# Revit family: Domotics-DomesticRanges-GEWISS-SYSTEM_ENCLOSURE-WATERTIGHT-IP65
name_source: partatom
category: Apparecchi elettrici
revit_build: Autodesk Revit 2016 (Build: 20161004_0715(x64)
units: mm (PartAtom-declared; Revit-internal decimal feet)

## family parameters
Condiviso = No
Host = Superficie
Mantenere orientamento annotazione = Sì
Punto di calcolo locali = Sì
Quota connettore circolare = Usa diametro
Taglio con vuoti quando caricato = No
Tipo di parte = Normale

## types (1)
- Domotics-DomesticRanges-GEWISS-SYSTEM_ENCLOSURE-WATERTIGHT-IP65
    Catalogue = DOMOTICS
    Catalogue Range = SYSTEM - BOXES
    Colour = Grey RAL 7035
    Description: = 2 gang
    Descrizione = WAT. IP65 ENCLOSURE 2M RIGID TRAN. COVER
    Door colour: = Smoked Transparent
    Door type = Rigid
    EAN code = 8011564856745
    Electrocod = 0212
    Glow Wire Test = 650°C
    IDF = 5ff36bd7-3460-49dc-94cf-c3dae0df500e
    IDT = 8f8934d9-406d-40ac-8908-5aafbfcae389
    IP degree = IP65
    Immagine tipo = GW27062.jpg
    Installation temperature = -25 +60 °C
    Insulation class = II
    Lid screws = Stainless steel
    Modello = GW27062
    N. holes Ã˜ 23 with cable gland = 1
    No. knockout holes Ã˜ 23 = 3
    No. knockout holes Ã˜23 = 4 on sides / 1 on the bottom
    Outer dim. LxHxD (mm) = 66x82x65
    Produttore = GEWISS S.p.A.
    Prospetto di default = 1219 mm
    SEO = Enclosure
    Shock resistance = IK07
    Standard = EN 60670-1
    Standard; = EN 60670-1
    Technical sheet = https://www.gewiss.com
    Thermo-pressure with ball = 70
    Torque screws tightening = 0,8NM
    Type of knockout holes = Removable with tool
    URL = https://www.gewiss.com
    Version file RFA = 19.4

note: source unit labels omitted for Thermo-pressure with ball — the stored unit's dimension contradicts the parameter name (converter mislabeling)
